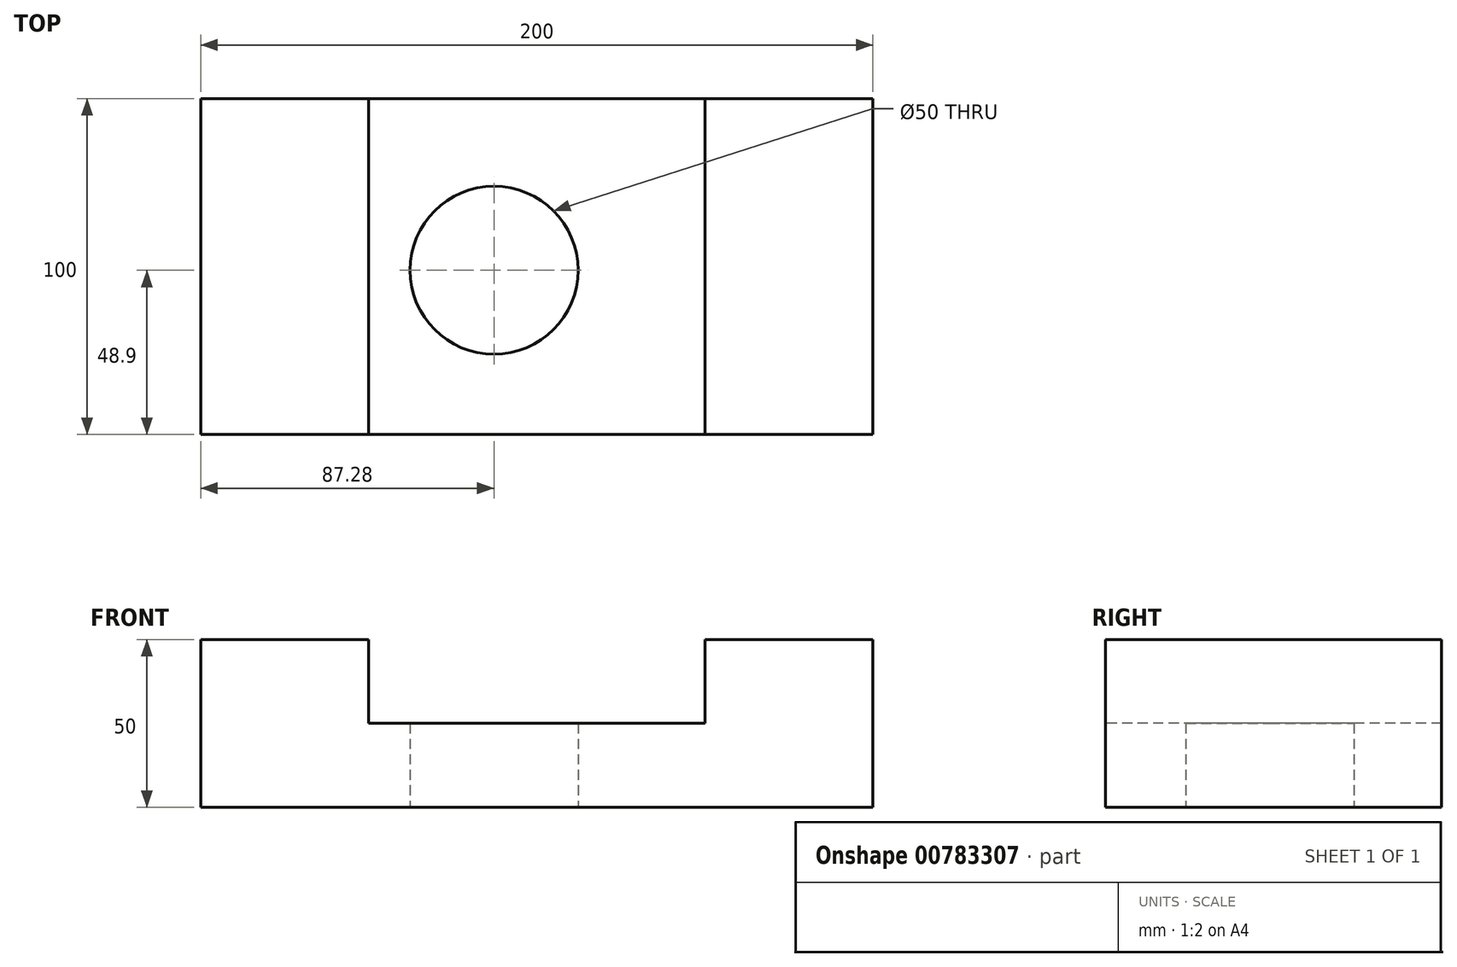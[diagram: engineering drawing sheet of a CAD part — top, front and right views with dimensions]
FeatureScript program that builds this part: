
annotation { "Feature Type Name" : "Feature", "Feature Type Description" : "" }
export const myFeature = defineFeature(function(context is Context, id is Id, definition is map)
    precondition{}
    {
        {
            var Q0;
            Q0=qCreatedBy(makeId("Top.planeOp"),FACE);
            var sketch = newSketch(context, id + "F0", { "sketchPlane" : qUnion([Q0])});
            skLineSegment(sketch, "E0.bottom", {"start": v(-87.28, 51.1) * mm, "end": v(112.72, 51.1) * mm});
            skLineSegment(sketch, "E0.top", {"start": v(-87.28, -48.9) * mm, "end": v(112.72, -48.9) * mm});
            skLineSegment(sketch, "E0.left", {"start": v(-87.28, 51.1) * mm, "end": v(-87.28, -48.9) * mm});
            skLineSegment(sketch, "E0.right", {"start": v(112.72, 51.1) * mm, "end": v(112.72, -48.9) * mm});
            skCircle(sketch, "E1", {"center": v(0, 0) * mm, "radius": 25 * mm});
            skSolve(sketch);
        }
        {
            var Q0;
            Q0=makeQuery(id+"F0.imprint","IMPRINT",FACE,{"disambiguationData":[TD([[makeQuery(id+"F0.imprint","IMPRINT",EDGE,{"derivedFrom":sQuery(id+"F0.wireOp",EDGE,"E0.bottom")}),-1.0]])]});
            var Q1;
            Q1 = qSketchRegion(id + "F2", true);
            extrude(context, id + "F1", {"entities" : qUnion([Q0, Q1]), "depth" : 50 * mm, "offsetDistance" : 25 * mm});
        }
        {
            var Q0;
            Q0=makeQuery(id+"F1.opExtrude","CAP_FACE",FACE,{"disambiguationData":[OSD([sQuery(id+"F0.wireOp",EDGE,"E0.bottom"),sQuery(id+"F0.wireOp",EDGE,"E0.top"),sQuery(id+"F0.wireOp",EDGE,"E0.left"),sQuery(id+"F0.wireOp",EDGE,"E0.right")])],"isStart":false});
            var sketch = newSketch(context, id + "F2", { "sketchPlane" : qUnion([Q0])});
            skLineSegment(sketch, "E2.bottom", {"start": v(-37.28, 51.1) * mm, "end": v(62.72, 51.1) * mm});
            skLineSegment(sketch, "E2.top", {"start": v(-37.28, -48.9) * mm, "end": v(62.72, -48.9) * mm});
            skLineSegment(sketch, "E2.left", {"start": v(-37.28, 51.1) * mm, "end": v(-37.28, -48.9) * mm});
            skLineSegment(sketch, "E2.right", {"start": v(62.72, 51.1) * mm, "end": v(62.72, -48.9) * mm});
            skSolve(sketch);
        }
        {
            var Q0;
            Q0=makeQuery(id+"F2.imprint","IMPRINT",FACE,{"disambiguationData":[TD([[makeQuery(id+"F2.imprint","IMPRINT",EDGE,{"derivedFrom":sQuery(id+"F2.wireOp",EDGE,"E2.bottom")}),-1.0]])]});
            extrude(context, id + "F3", {"entities" : qUnion([Q0]), "operationType" : NewBodyOperationType.REMOVE, "oppositeDirection" : true, "depth" : 25 * mm, "offsetDistance" : 25 * mm});
        }
    });
